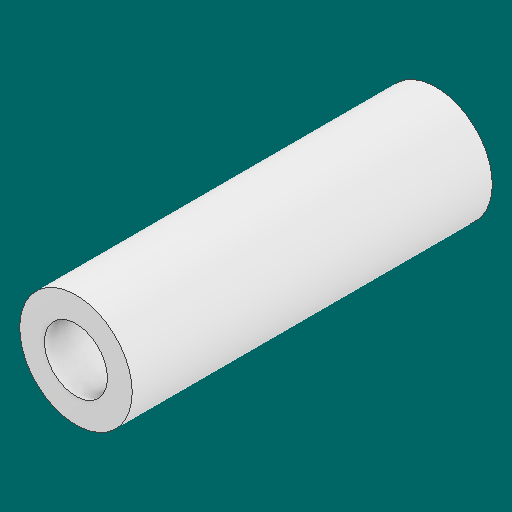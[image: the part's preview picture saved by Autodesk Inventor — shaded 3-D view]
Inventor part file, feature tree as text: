
AUTODESK INVENTOR PART (.ipt)
format: ipt  version: 2023.1 (Build 271208000, 208)  size: 97,280 bytes
history: native  units: in
note: dims shown in document units (in); Inventor stores cm internally (conversion verified against a paired STEP export)
features: other x3, sketch x1
ambient origin geometry x8: Origin, YZ Plane, XZ Plane, XY Plane, X Axis, Y Axis, Z Axis, Center Point
bodies: Solid1 (feature_tree)
feature tree (4):
  other  "1.2inSpacer.ipt"
  other  "Solid1::1.2inSpacer.ipt"
  other  "TaggingFeature1"
  sketch  "Sketch1"  dims[d0=0.3937in]
